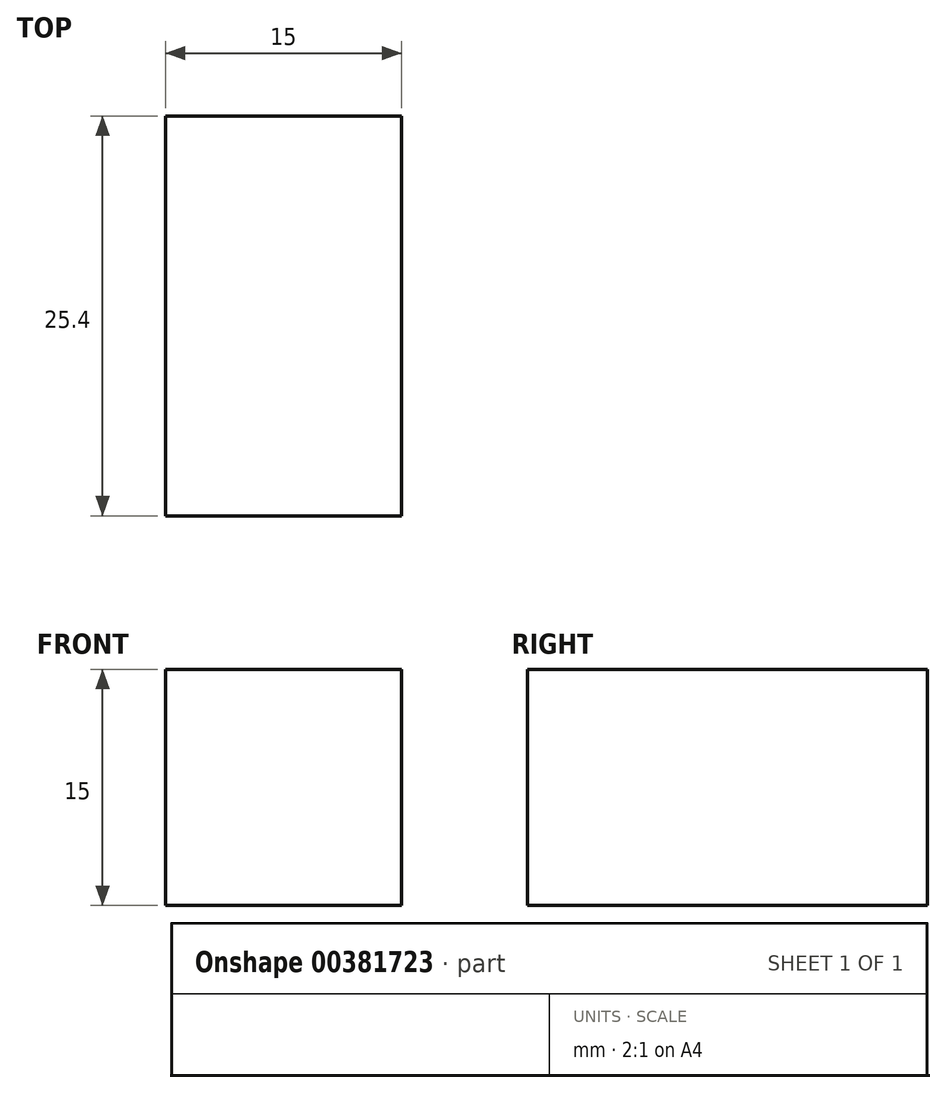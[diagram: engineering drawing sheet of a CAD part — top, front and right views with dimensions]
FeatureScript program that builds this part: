
annotation { "Feature Type Name" : "Feature", "Feature Type Description" : "" }
export const myFeature = defineFeature(function(context is Context, id is Id, definition is map)
    precondition{}
    {
        {
            var Q0;
            Q0=qCreatedBy(makeId("Front.planeOp"),FACE);
            var sketch = newSketch(context, id + "F0", { "sketchPlane" : qUnion([Q0])});
            skLineSegment(sketch, "E0", {"start": v(0, 0) * mm, "end": v(15, 0) * mm});
            skLineSegment(sketch, "E1", {"start": v(15, 0) * mm, "end": v(15, 15) * mm});
            skLineSegment(sketch, "E2", {"start": v(15, 15) * mm, "end": v(0, 15) * mm});
            skLineSegment(sketch, "E3", {"start": v(0, 0) * mm, "end": v(0, 15) * mm});
            skSolve(sketch);
        }
        {
            var Q0;
            Q0 = qSketchRegion(id + "F0", true);
            extrude(context, id + "F1", {"entities" : qUnion([Q0]), "depth" : 25.4 * mm});
        }
    });
